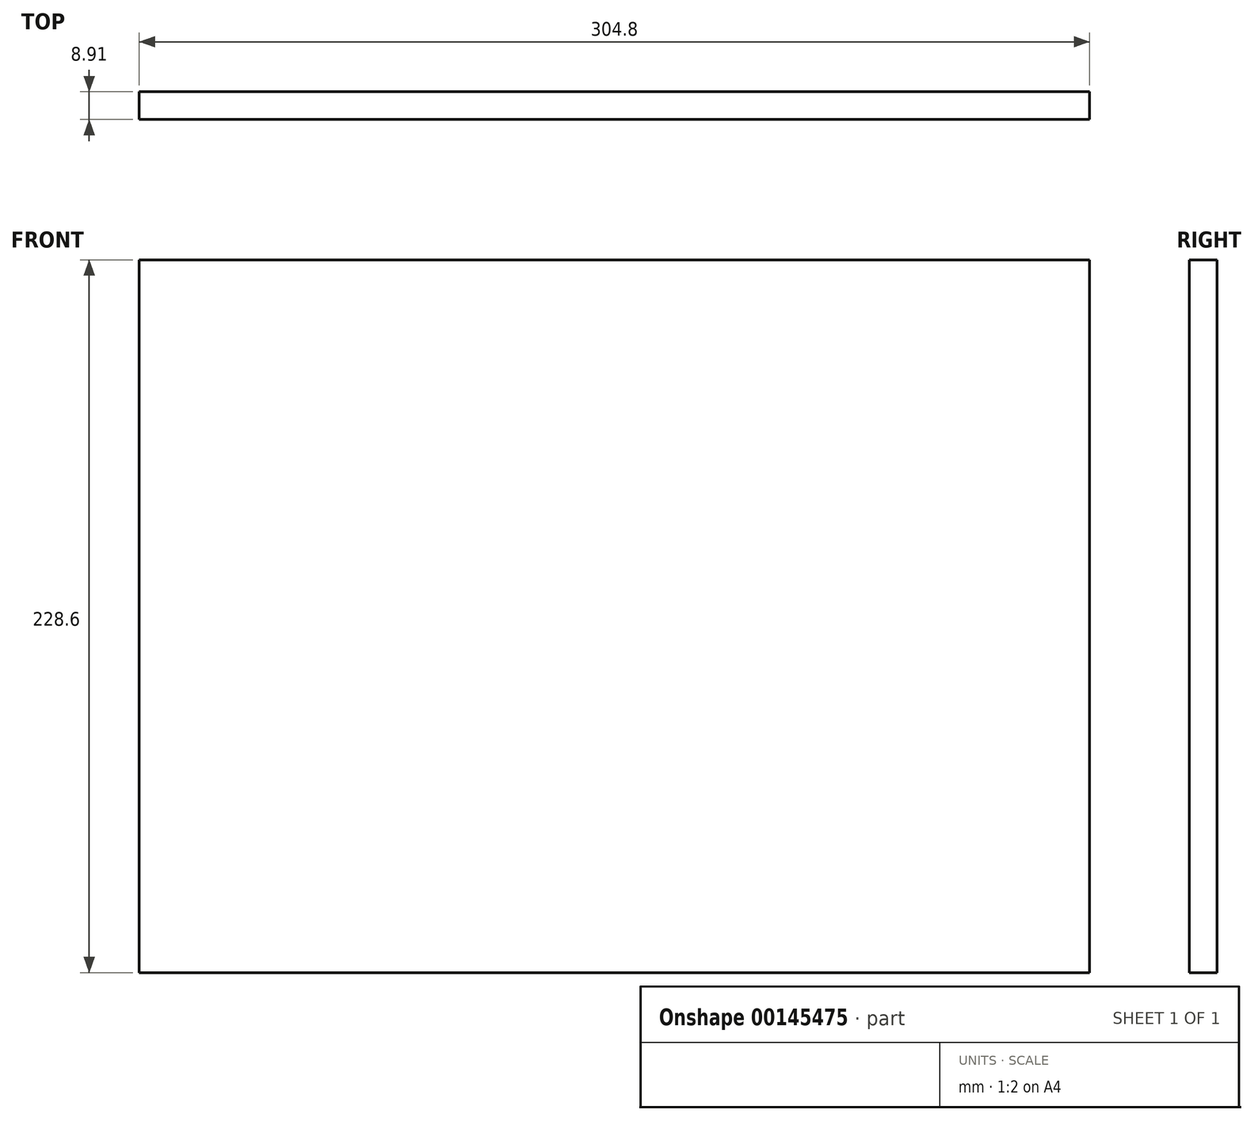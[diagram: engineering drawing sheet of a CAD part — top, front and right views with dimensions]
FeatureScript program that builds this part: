
annotation { "Feature Type Name" : "Feature", "Feature Type Description" : "" }
export const myFeature = defineFeature(function(context is Context, id is Id, definition is map)
    precondition{}
    {
        {
            var Q0;
            Q0=qCreatedBy(makeId("Front.planeOp"),FACE);
            var sketch = newSketch(context, id + "F0", { "sketchPlane" : qUnion([Q0])});
            skLineSegment(sketch, "E0.bottom", {"start": v(-176, 109.2) * mm, "end": v(128.8, 109.2) * mm});
            skLineSegment(sketch, "E0.top", {"start": v(-176, -119.4) * mm, "end": v(128.8, -119.4) * mm});
            skLineSegment(sketch, "E0.left", {"start": v(-176, 109.2) * mm, "end": v(-176, -119.4) * mm});
            skLineSegment(sketch, "E0.right", {"start": v(128.8, 109.2) * mm, "end": v(128.8, -119.4) * mm});
            skSolve(sketch);
        }
        {
            var Q0;
            Q0=makeQuery(id+"F0.imprint","IMPRINT",FACE,{"disambiguationData":[TD([[makeQuery(id+"F0.imprint","IMPRINT",EDGE,{"derivedFrom":sQuery(id+"F0.wireOp",EDGE,"E0.bottom")}),-1.0]])]});
            extrude(context, id + "F1", {"entities" : qUnion([Q0]), "depth" : 8.9 * mm});
        }
    });
